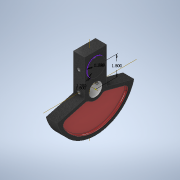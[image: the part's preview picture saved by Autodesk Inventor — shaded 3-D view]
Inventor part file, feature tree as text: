
AUTODESK INVENTOR PART (.ipt)
format: ipt  version: 2021.1 (Build 251245000, 245)  size: 264,192 bytes
history: native  units: in
note: dims shown in document units (in); Inventor stores cm internally (conversion verified against a paired STEP export)
features: extrude x7, sketch x5, projected_geometry x5, mirror x1, fillet x1
ambient origin geometry x8: Origin, YZ Plane, XZ Plane, XY Plane, X Axis, Y Axis, Z Axis, Center Point
bodies: Solid1 (feature_tree)
feature tree (19):
  extrude  "Extrusion1"  Depth=1.2in
  sketch  "Sketch2"  dims[d8=1.6in d9=0.0in d10=0.0in]
  extrude  "Extrusion2"  TaperAngle=0.0deg  [1 undecoded]
  extrude  "Extrusion3"  Depth=1.2in
  sketch  "Sketch3"  dims[d11=0.1in d12=0.0in d13=1.2in]
  extrude  "Extrusion4"  Depth=1.8in
  extrude  "Extrusion5"  Depth=0.1in TaperAngle=0.0deg
  extrude  "Extrusion6"  Depth=0.1in
  mirror  "Mirror1"
  extrude  "Extrusion7"  Depth=0.3in
  fillet  "Fillet1"  Radius=0.3in
  sketch  "Sketch1"  dims[d5=1.0in d6=0.0in d7=1.2in]
  sketch  "Sketch4"  dims[d14=1.6in d15=1.8in]
  projected_geometry  "Projected Loop1"
  sketch  "Sketch5"  dims[d16=0.0in d17=0.0in d18=0.1in d19=0.0in d20=6.6in d21=0.3in d22=0.3in d23=0.4in d24=1.7in d25=0.4in d26=0.2in d27=0.0in d28=0.3in d29=0.3in d30=0.0in d31=0.0in d32=0.1in]
  projected_geometry  "Projected Loop2"
  projected_geometry  "Projected Loop3"
  projected_geometry  "Project Cut Edges1"
  projected_geometry  "Project Cut Edges2"
note: 1 required parameter value undecoded (feature->parameter linkage not recoverable at this tier; creation-order binding heuristic only, values carry confidence <= 0.55)
